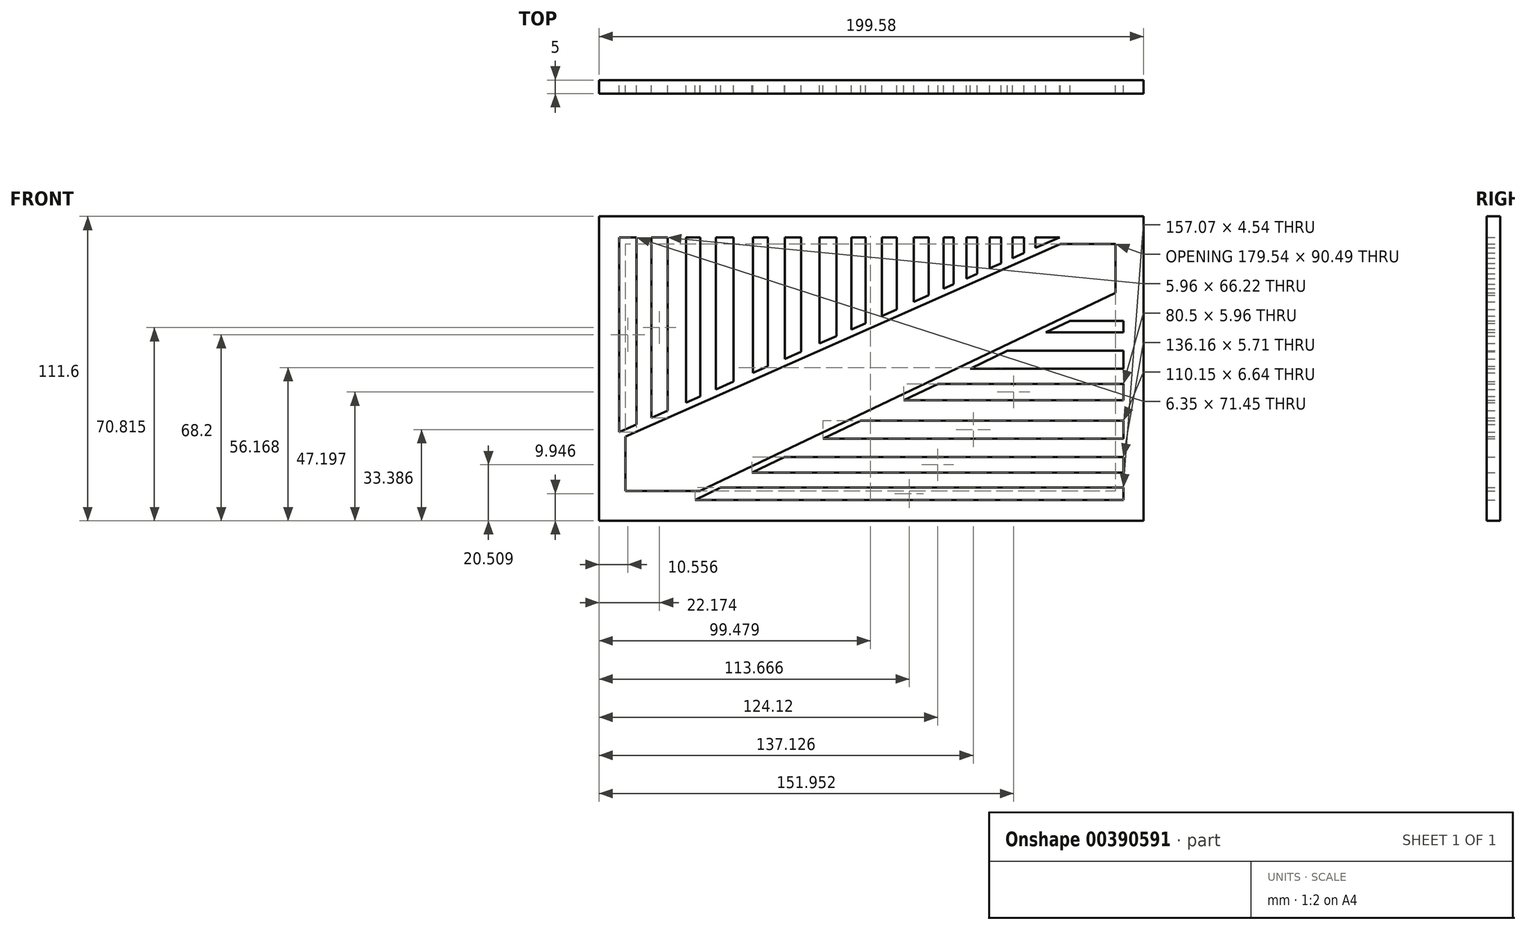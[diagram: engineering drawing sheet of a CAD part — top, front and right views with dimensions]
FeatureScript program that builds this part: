
annotation { "Feature Type Name" : "Feature", "Feature Type Description" : "" }
export const myFeature = defineFeature(function(context is Context, id is Id, definition is map)
    precondition{}
    {
        {
            var Q0;
            Q0=qCreatedBy(makeId("Front.planeOp"),FACE);
            var sketch = newSketch(context, id + "F0", { "sketchPlane" : qUnion([Q0])});
            skLineSegment(sketch, "E0.bottom", {"start": v(-99.8, 55.8) * mm, "end": v(99.8, 55.8) * mm});
            skLineSegment(sketch, "E0.top", {"start": v(-99.8, -55.8) * mm, "end": v(99.8, -55.8) * mm});
            skLineSegment(sketch, "E0.left", {"start": v(-99.8, 55.8) * mm, "end": v(-99.8, -55.8) * mm});
            skLineSegment(sketch, "E0.right", {"start": v(99.8, 55.8) * mm, "end": v(99.8, -55.8) * mm});
            skPoint(sketch, "E0.middle", {"position": v(0, 0) * mm});
            skLineSegment(sketch, "E1.bottom", {"start": v(-92.41, 48.12) * mm, "end": v(-86.06, 48.12) * mm});
            skLineSegment(sketch, "E1.top", {"start": v(-92.41, -48.12) * mm, "end": v(92.41, -48.12) * mm});
            skLineSegment(sketch, "E1.left", {"start": v(-92.41, 48.12) * mm, "end": v(-92.41, -48.12) * mm});
            skLineSegment(sketch, "E1.right", {"start": v(92.41, 48.12) * mm, "end": v(92.41, 26.83) * mm});
            skLineSegment(sketch, "E2", {"start": v(-90.08, -24.95) * mm, "end": v(69.32, 45.61) * mm});
            skLineSegment(sketch, "E3", {"start": v(-62.87, -44.88) * mm, "end": v(89.46, 27.82) * mm});
            skLineSegment(sketch, "E4", {"start": v(-64.66, -48.12) * mm, "end": v(-55.14, -43.58) * mm});
            skLineSegment(sketch, "E5", {"start": v(-92.41, -23.32) * mm, "end": v(-86.06, -20.51) * mm});
            skLineSegment(sketch, "E6", {"start": v(-90.08, -24.95) * mm, "end": v(-90.08, -44.88) * mm});
            skLineSegment(sketch, "E7", {"start": v(69.32, 45.61) * mm, "end": v(89.46, 45.61) * mm});
            skLineSegment(sketch, "E8", {"start": v(89.46, 45.61) * mm, "end": v(89.46, 27.82) * mm});
            skLineSegment(sketch, "E9", {"start": v(-90.08, -44.88) * mm, "end": v(-62.87, -44.88) * mm});
            skPoint(sketch, "E10.orphan", {"position": v(92.41, 29.23) * mm});
            skPoint(sketch, "E11.orphan", {"position": v(75, 48.12) * mm});
            skLineSegment(sketch, "E12", {"start": v(-86.06, 48.12) * mm, "end": v(-86.06, -20.51) * mm});
            skLineSegment(sketch, "E13", {"start": v(-80.6, 48.12) * mm, "end": v(-80.6, -18.1) * mm});
            skLineSegment(sketch, "E14", {"start": v(-74.64, 48.12) * mm, "end": v(-74.64, -15.46) * mm});
            skLineSegment(sketch, "E15", {"start": v(-67.93, 48.12) * mm, "end": v(-67.93, -12.49) * mm});
            skLineSegment(sketch, "E16", {"start": v(-62.72, 48.12) * mm, "end": v(-62.72, -10.18) * mm});
            skLineSegment(sketch, "E17", {"start": v(-57, 48.12) * mm, "end": v(-57, -7.65) * mm});
            skLineSegment(sketch, "E18", {"start": v(-50.55, 48.12) * mm, "end": v(-50.55, -4.8) * mm});
            skLineSegment(sketch, "E19", {"start": v(-43.36, 48.12) * mm, "end": v(-43.36, -1.6) * mm});
            skLineSegment(sketch, "E20", {"start": v(-37.9, 48.12) * mm, "end": v(-37.9, 0.8) * mm});
            skLineSegment(sketch, "E21", {"start": v(-31.69, 48.12) * mm, "end": v(-31.69, 3.56) * mm});
            skLineSegment(sketch, "E22", {"start": v(-25.73, 48.12) * mm, "end": v(-25.73, 6.2) * mm});
            skLineSegment(sketch, "E23", {"start": v(-19.03, 48.12) * mm, "end": v(-19.03, 9.16) * mm});
            skLineSegment(sketch, "E24", {"start": v(-12.82, 48.12) * mm, "end": v(-12.82, 11.9) * mm});
            skLineSegment(sketch, "E25", {"start": v(-7.36, 48.12) * mm, "end": v(-7.36, 14.33) * mm});
            skLineSegment(sketch, "E26", {"start": v(-2.14, 48.12) * mm, "end": v(-2.14, 16.64) * mm});
            skLineSegment(sketch, "E27", {"start": v(3.82, 48.12) * mm, "end": v(3.82, 19.27) * mm});
            skLineSegment(sketch, "E28", {"start": v(9.28, 48.12) * mm, "end": v(9.28, 21.7) * mm});
            skLineSegment(sketch, "E29", {"start": v(15.48, 48.12) * mm, "end": v(15.48, 24.44) * mm});
            skLineSegment(sketch, "E30", {"start": v(20.95, 48.12) * mm, "end": v(20.95, 26.86) * mm});
            skLineSegment(sketch, "E31", {"start": v(26.4, 48.12) * mm, "end": v(26.4, 29.27) * mm});
            skLineSegment(sketch, "E32", {"start": v(30.13, 48.12) * mm, "end": v(30.13, 30.92) * mm});
            skLineSegment(sketch, "E33", {"start": v(34.85, 48.12) * mm, "end": v(34.85, 33.01) * mm});
            skLineSegment(sketch, "E34", {"start": v(38.82, 48.12) * mm, "end": v(38.82, 34.77) * mm});
            skLineSegment(sketch, "E35", {"start": v(43.29, 48.12) * mm, "end": v(43.29, 36.75) * mm});
            skLineSegment(sketch, "E36", {"start": v(47.51, 48.12) * mm, "end": v(47.51, 38.62) * mm});
            skLineSegment(sketch, "E37", {"start": v(51.73, 48.12) * mm, "end": v(51.73, 40.48) * mm});
            skLineSegment(sketch, "E38", {"start": v(55.95, 48.12) * mm, "end": v(55.95, 42.35) * mm});
            skLineSegment(sketch, "E39", {"start": v(60.17, 48.12) * mm, "end": v(60.17, 44.22) * mm});
            skLineSegment(sketch, "E40", {"start": v(-55.14, -43.58) * mm, "end": v(92.41, -43.58) * mm});
            skLineSegment(sketch, "E41", {"start": v(92.41, -38.15) * mm, "end": v(-43.75, -38.15) * mm});
            skLineSegment(sketch, "E42", {"start": v(92.41, -32.44) * mm, "end": v(-31.78, -32.44) * mm});
            skLineSegment(sketch, "E43", {"start": v(92.41, -25.73) * mm, "end": v(-17.74, -25.73) * mm});
            skPoint(sketch, "E44.endSnap0", {"position": v(13.88, -10.65) * mm});
            skLineSegment(sketch, "E45", {"start": v(92.41, -11.58) * mm, "end": v(11.91, -11.58) * mm});
            skLineSegment(sketch, "E46", {"start": v(92.41, -5.62) * mm, "end": v(24.4, -5.62) * mm});
            skLineSegment(sketch, "E47", {"start": v(92.41, 0) * mm, "end": v(36.18, 0) * mm});
            skLineSegment(sketch, "E48", {"start": v(92.41, 6.54) * mm, "end": v(49.9, 6.54) * mm});
            skLineSegment(sketch, "E49", {"start": v(92.41, 13.24) * mm, "end": v(63.94, 13.24) * mm});
            skLineSegment(sketch, "E50", {"start": v(92.41, 17.47) * mm, "end": v(72.78, 17.47) * mm});
            skLineSegment(sketch, "E51", {"start": v(92.41, 23.18) * mm, "end": v(84.75, 23.18) * mm});
            skLineSegment(sketch, "E52.trimOffspring", {"start": v(-80.6, 48.12) * mm, "end": v(-74.64, 48.12) * mm});
            skLineSegment(sketch, "E53.trimOffspring", {"start": v(-67.93, 48.12) * mm, "end": v(-62.72, 48.12) * mm});
            skLineSegment(sketch, "E54.trimOffspring", {"start": v(-57, 48.12) * mm, "end": v(-50.55, 48.12) * mm});
            skLineSegment(sketch, "E55.trimOffspring", {"start": v(-43.36, 48.12) * mm, "end": v(-37.9, 48.12) * mm});
            skLineSegment(sketch, "E56.trimOffspring", {"start": v(-31.69, 48.12) * mm, "end": v(-25.73, 48.12) * mm});
            skLineSegment(sketch, "E57.trimOffspring", {"start": v(-19.03, 48.12) * mm, "end": v(-12.82, 48.12) * mm});
            skLineSegment(sketch, "E58.trimOffspring", {"start": v(-7.36, 48.12) * mm, "end": v(-2.14, 48.12) * mm});
            skLineSegment(sketch, "E59.trimOffspring", {"start": v(3.82, 48.12) * mm, "end": v(9.28, 48.12) * mm});
            skLineSegment(sketch, "E60.trimOffspring", {"start": v(15.48, 48.12) * mm, "end": v(20.95, 48.12) * mm});
            skLineSegment(sketch, "E61.trimOffspring", {"start": v(26.4, 48.12) * mm, "end": v(30.13, 48.12) * mm});
            skLineSegment(sketch, "E62.trimOffspring", {"start": v(34.85, 48.12) * mm, "end": v(38.82, 48.12) * mm});
            skLineSegment(sketch, "E63.trimOffspring", {"start": v(43.29, 48.12) * mm, "end": v(47.51, 48.12) * mm});
            skLineSegment(sketch, "E64.trimOffspring", {"start": v(51.73, 48.12) * mm, "end": v(55.95, 48.12) * mm});
            skLineSegment(sketch, "E65.trimOffspring", {"start": v(60.17, 48.12) * mm, "end": v(92.41, 48.12) * mm});
            skLineSegment(sketch, "E66.trimOffspring", {"start": v(60.17, 44.22) * mm, "end": v(68.99, 48.12) * mm});
            skLineSegment(sketch, "E67.trimOffspring", {"start": v(51.73, 40.48) * mm, "end": v(55.95, 42.35) * mm});
            skLineSegment(sketch, "E68.trimOffspring", {"start": v(43.29, 36.75) * mm, "end": v(47.51, 38.62) * mm});
            skLineSegment(sketch, "E69.trimOffspring", {"start": v(34.85, 33.01) * mm, "end": v(38.82, 34.77) * mm});
            skLineSegment(sketch, "E70.trimOffspring", {"start": v(26.4, 29.27) * mm, "end": v(30.13, 30.92) * mm});
            skLineSegment(sketch, "E71.trimOffspring", {"start": v(15.48, 24.44) * mm, "end": v(20.95, 26.86) * mm});
            skLineSegment(sketch, "E72.trimOffspring", {"start": v(3.82, 19.27) * mm, "end": v(9.28, 21.7) * mm});
            skLineSegment(sketch, "E73.trimOffspring", {"start": v(-7.36, 14.33) * mm, "end": v(-2.14, 16.64) * mm});
            skLineSegment(sketch, "E74.trimOffspring", {"start": v(-19.03, 9.16) * mm, "end": v(-12.82, 11.9) * mm});
            skLineSegment(sketch, "E75.trimOffspring", {"start": v(-31.69, 3.56) * mm, "end": v(-25.73, 6.2) * mm});
            skLineSegment(sketch, "E76.trimOffspring", {"start": v(-43.36, -1.6) * mm, "end": v(-37.9, 0.8) * mm});
            skLineSegment(sketch, "E77.trimOffspring", {"start": v(-57, -7.65) * mm, "end": v(-50.55, -4.8) * mm});
            skLineSegment(sketch, "E78.trimOffspring", {"start": v(-67.93, -12.49) * mm, "end": v(-62.72, -10.18) * mm});
            skLineSegment(sketch, "E79.trimOffspring", {"start": v(-80.6, -18.1) * mm, "end": v(-74.64, -15.46) * mm});
            skLineSegment(sketch, "E80.trimOffspring", {"start": v(-43.75, -38.15) * mm, "end": v(-31.78, -32.44) * mm});
            skLineSegment(sketch, "E81.trimOffspring", {"start": v(-17.74, -25.73) * mm, "end": v(-3.83, -19.1) * mm});
            skLineSegment(sketch, "E82.trimOffspring", {"start": v(11.91, -11.58) * mm, "end": v(24.4, -5.62) * mm});
            skLineSegment(sketch, "E83.trimOffspring", {"start": v(36.18, 0) * mm, "end": v(49.9, 6.54) * mm});
            skLineSegment(sketch, "E84.trimOffspring", {"start": v(63.94, 13.24) * mm, "end": v(72.78, 17.47) * mm});
            skLineSegment(sketch, "E85.trimOffspring", {"start": v(84.75, 23.18) * mm, "end": v(92.41, 26.83) * mm});
            skLineSegment(sketch, "E86.trimOffspring", {"start": v(92.41, 17.47) * mm, "end": v(92.41, 13.24) * mm});
            skLineSegment(sketch, "E87.trimOffspring", {"start": v(92.41, 6.54) * mm, "end": v(92.41, 0) * mm});
            skLineSegment(sketch, "E88.trimOffspring", {"start": v(92.41, -5.62) * mm, "end": v(92.41, -11.58) * mm});
            skLineSegment(sketch, "E89.trimOffspring", {"start": v(92.41, -19.1) * mm, "end": v(92.41, -25.73) * mm});
            skLineSegment(sketch, "E90.trimOffspring", {"start": v(92.41, -32.44) * mm, "end": v(92.41, -38.15) * mm});
            skLineSegment(sketch, "E91.trimOffspring", {"start": v(92.41, -43.58) * mm, "end": v(92.41, -48.12) * mm});
            skLineSegment(sketch, "E92", {"start": v(92.41, -19.1) * mm, "end": v(-3.83, -19.1) * mm});
            skSolve(sketch);
        }
        {
            var Q0;
            Q0 = qSketchRegion(id + "F0", true);
            extrude(context, id + "F1", {"entities" : qUnion([Q0]), "depth" : 5 * mm});
        }
    });
